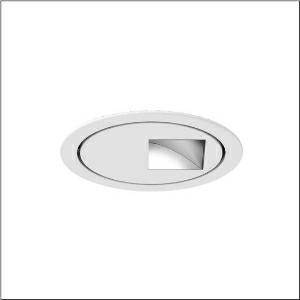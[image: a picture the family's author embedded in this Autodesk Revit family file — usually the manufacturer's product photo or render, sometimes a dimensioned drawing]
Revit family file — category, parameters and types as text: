
# Revit family: lunis_11_mini_round_51dk11b72wn21
name_source: partatom
category: Lighting Fixtures
units: mm (PartAtom-declared; Revit-internal decimal feet)

## family parameters
Cut with Voids When Loaded = No
Host = Face
Light Source = No
Part Type = Normal
Room Calculation Point = No
Round Connector Dimension = Use Diameter
Shared = No

## types (1)
- Lunis 11 mini round (1 x LED 4000K / CRI = 90 (unbekannt), 2120 lm, 4000K)
    Apparent Load = 28 VA
    CIE Flux Codes = 44 77 97 100 100
    Color Rendering = 90
    Color Temperature = 4000K
    Default Elevation = 1800 mm
    Description = Lunis 11 mini round, downlight, light control with wallwasher, of highly reflective aluminium, highly specular, light emission: direct distribution, LED rated luminous flux: 2.120lm, light colour: 940, control gear: ECG, with terminal, 3-pole, mains connection: 220..230V, AC/DC, 0/50..60Hz, LED module, luminaire module, of aluminium, highly specular, white, diameter: 176mm, clamping range: 1..40mm, recessing ring, of plastic, traffic white (RAL 9016), protection rating (complete): IP20, insulation class (complete): insulation class II (safety insulation), certification: CE, permissible ambient temperature for indoor applications: 0..+35°C, packaging unit: 1 piece
    Height = 0 mm  [stored 0 ft]
    Lamp = 1 x LED 4000K / CRI >= 90 (unbekannt)
    Lamp Light Flux = 2120 lm
    Lamp count = 1
    Length = 176 mm
    Luminous efficacy = 75 lm/W
    Manufacturer = Siteco
    ModVariant = No
    Model = 51DK11B72WN21
    Mounting Place = Ceiling
    Mounting Type = Recessed
    Number of Poles = 1
    OnlyDefault = Yes
    Power Factor = 1
    Product Name = Lunis 11 mini round
    Product group = downlight | ceiling recessed
    ProductGroupID = 402
    Protection Class = Protection class II
    Protection Degree = IP 20
    RLX_Detail_Level = 1
    RlxData = <blob elided: 59389 chars, md5=3648ada1>
    Socket = socket
    Standby Power = 0 W
    System Light Flux = 2120 lm
    System Power = 28 W
    Type Comments = Product without accessories
    Type Image = l_1004772.jpg
    URL = http://relux.com
    VarID = ---
    Voltage = 0 V
    Weight = 0.00 kg
    Width = 176 mm

note: [stored X ft] marks values corroborated as IEEE doubles in the binary element streams (Revit-internal decimal feet)

## geometry (parser evidence)
native form markers: Blend x4, Sweep x10
no freeform markers — native parametric forms only
